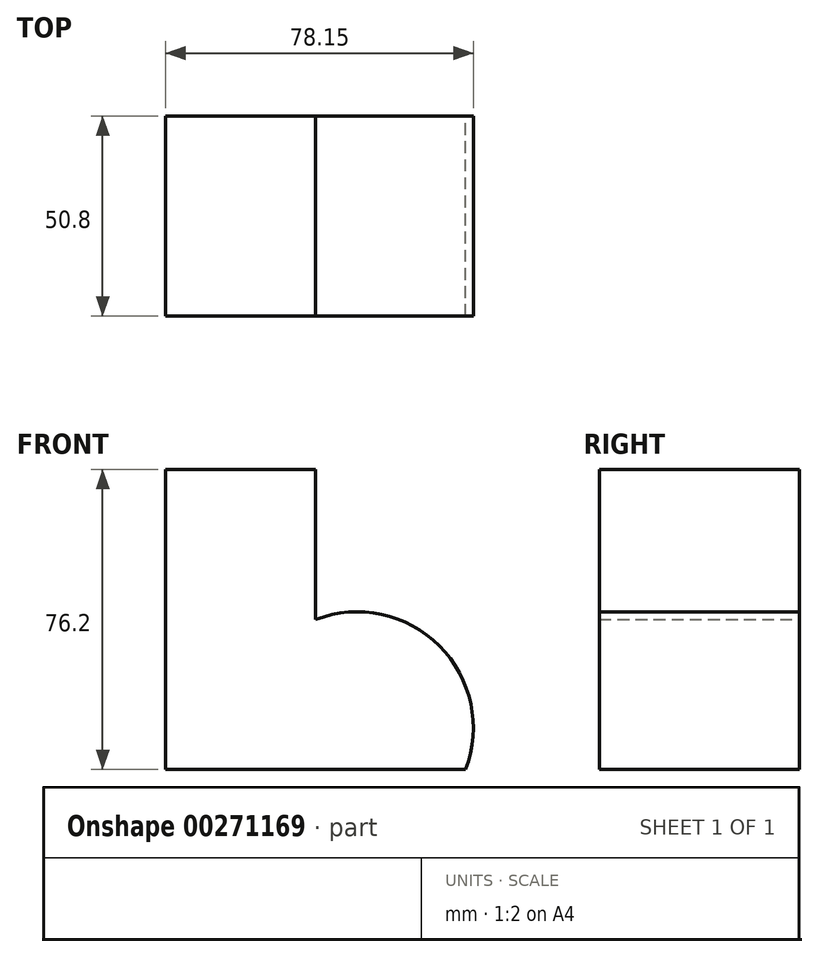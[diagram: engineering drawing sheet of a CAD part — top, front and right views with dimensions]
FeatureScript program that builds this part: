
annotation { "Feature Type Name" : "Feature", "Feature Type Description" : "" }
export const myFeature = defineFeature(function(context is Context, id is Id, definition is map)
    precondition{}
    {
        {
            var Q0;
            Q0=qCreatedBy(makeId("Front.planeOp"),FACE);
            var sketch = newSketch(context, id + "F0", { "sketchPlane" : qUnion([Q0])});
            skLineSegment(sketch, "E0", {"start": v(0, 0) * mm, "end": v(-76.38, 0) * mm});
            skLineSegment(sketch, "E1", {"start": v(0, 0) * mm, "end": v(-76.2, 0) * mm});
            skLineSegment(sketch, "E2", {"start": v(-76.2, 0) * mm, "end": v(-76.2, 76.2) * mm});
            skLineSegment(sketch, "E3", {"start": v(-76.2, 76.2) * mm, "end": v(-38.1, 76.2) * mm});
            skLineSegment(sketch, "E4", {"start": v(-38.1, 76.2) * mm, "end": v(-38.1, 38.1) * mm});
            skArc(sketch, "E5", {"start": v(0, 0) * mm, "mid": v(-6.7, 31.4) * mm, "end": v(-38.1, 38.1) * mm});
            skSolve(sketch);
        }
        {
            var Q0;
            Q0 = qSketchRegion(id + "F0", true);
            extrude(context, id + "F1", {"entities" : qUnion([Q0]), "depth" : 50.8 * mm});
        }
    });
